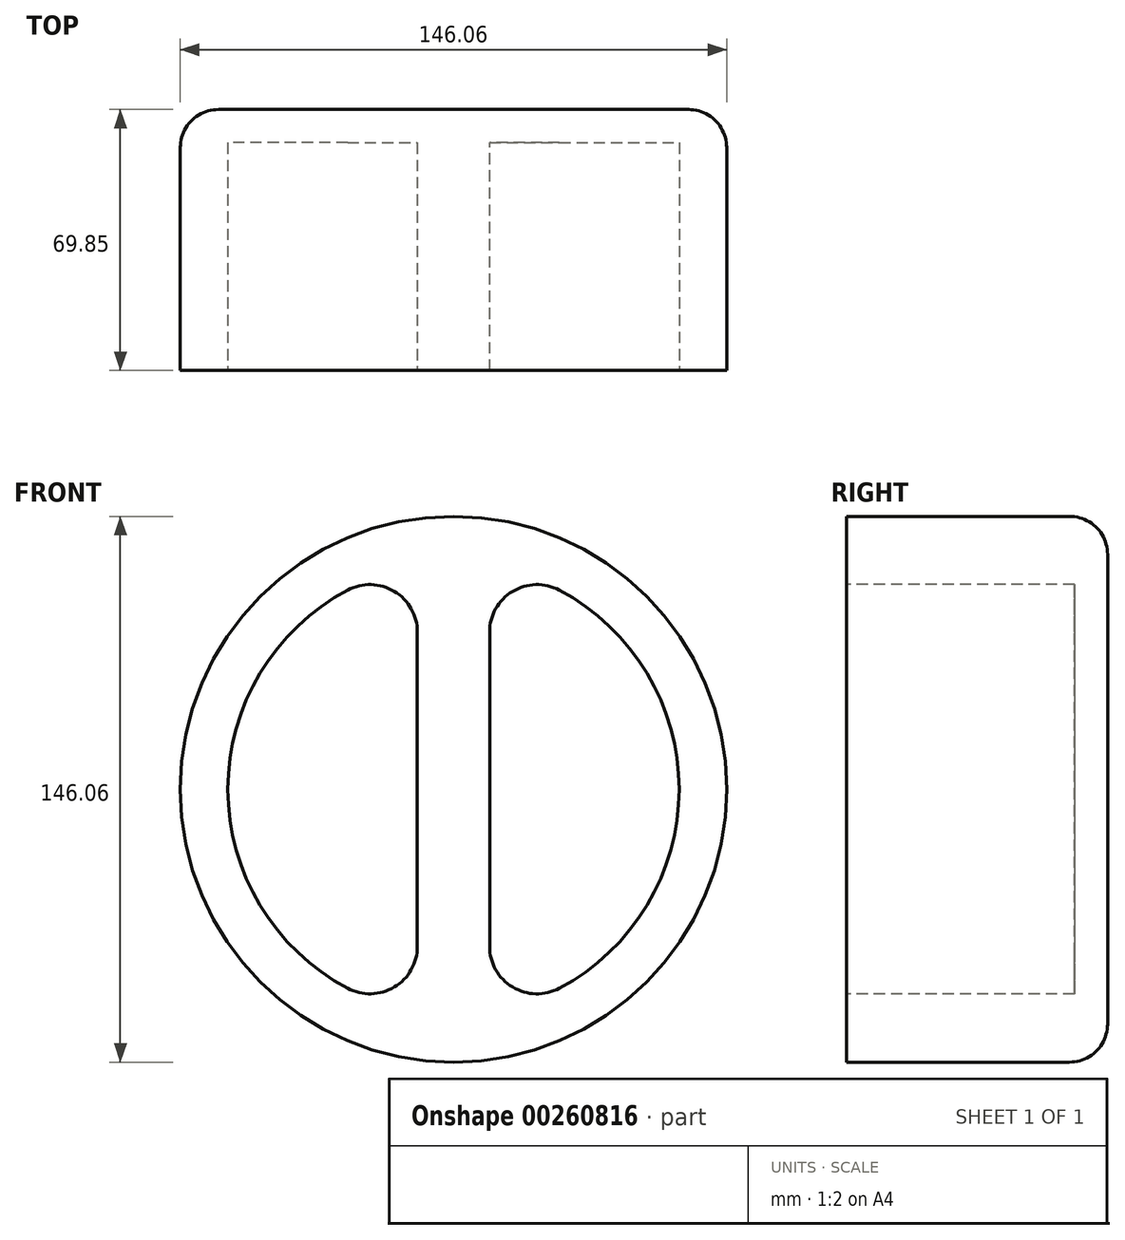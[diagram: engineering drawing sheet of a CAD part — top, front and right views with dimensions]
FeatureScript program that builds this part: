
annotation { "Feature Type Name" : "Feature", "Feature Type Description" : "" }
export const myFeature = defineFeature(function(context is Context, id is Id, definition is map)
    precondition{}
    {
        {
            var Q0;
            Q0=qCreatedBy(makeId("Front.planeOp"),FACE);
            var sketch = newSketch(context, id + "F0", { "sketchPlane" : qUnion([Q0])});
            skCircle(sketch, "E0", {"center": v(0, 0) * mm, "radius": 73.02 * mm});
            skSolve(sketch);
        }
        {
            var Q0;
            Q0=makeQuery(id+"F0.imprint","IMPRINT",FACE,{"disambiguationData":[TD([[makeQuery(id+"F0.imprint","IMPRINT",EDGE,{"derivedFrom":sQuery(id+"F0.wireOp",EDGE,"E0")}),1.0]])]});
            extrude(context, id + "F1", {"entities" : qUnion([Q0]), "depth" : 69.85 * mm});
        }
        {
            var Q0;
            Q0=makeQuery(id+"F1.opExtrude","CAP_FACE",FACE,{"disambiguationData":[OSD([sQuery(id+"F0.wireOp",EDGE,"E0")])],"isStart":false});
            var sketch = newSketch(context, id + "F2", { "sketchPlane" : qUnion([Q0])});
            skCircle(sketch, "E1", {"center": v(0, 0) * mm, "radius": 60.33 * mm});
            skLineSegment(sketch, "E2", {"start": v(-9.65, 59.55) * mm, "end": v(-9.65, -59.55) * mm});
            skLineSegment(sketch, "E3", {"start": v(9.65, 59.55) * mm, "end": v(9.65, -59.55) * mm});
            skSolve(sketch);
        }
        {
            var Q0;
            {var subQ0=sQuery(id+"F2.wireOp",EDGE,"E2");Q0=makeQuery(id+"F2.imprint","IMPRINT",FACE,{"disambiguationData":[TD([[makeQuery(id+"F2.imprint","IMPRINT",EDGE,{"derivedFrom":subQ0}),-1.0]])]});}
            var Q1;
            {var subQ0=sQuery(id+"F2.wireOp",EDGE,"E3");Q1=makeQuery(id+"F2.imprint","IMPRINT",FACE,{"disambiguationData":[TD([[makeQuery(id+"F2.imprint","IMPRINT",EDGE,{"derivedFrom":subQ0}),1.0]])]});}
            extrude(context, id + "F3", {"entities" : qUnion([Q0, Q1]), "operationType" : NewBodyOperationType.REMOVE, "oppositeDirection" : true, "depth" : 60.96 * mm});
        }
        {
            var Q0;
            {var subQ0=sQuery(id+"F2.wireOp",EDGE,"E3");var subQ1=sQuery(id+"F2.wireOp",EDGE,"E1");Q0=makeQuery(id+"F3.boolean.opBoolean","COPY",EDGE,{"derivedFrom":makeQuery(id+"F3.opExtrude","SWEPT_EDGE",EDGE,{"disambiguationData":[OSD([subQ1,subQ0]),TDD([makeQuery(id+"F2.imprint","INTERSECT",VERTEX,{"disambiguationData":[OD(0.0)],"derivedFrom":[subQ1,subQ0]})])]})});}
            var Q1;
            {var subQ0=sQuery(id+"F2.wireOp",EDGE,"E2");var subQ1=sQuery(id+"F2.wireOp",EDGE,"E1");Q1=makeQuery(id+"F3.boolean.opBoolean","COPY",EDGE,{"derivedFrom":makeQuery(id+"F3.opExtrude","SWEPT_EDGE",EDGE,{"disambiguationData":[OSD([subQ1,subQ0]),TDD([makeQuery(id+"F2.imprint","INTERSECT",VERTEX,{"disambiguationData":[OD(0.0)],"derivedFrom":[subQ1,subQ0]})])]})});}
            var Q2;
            {var subQ0=sQuery(id+"F2.wireOp",EDGE,"E3");var subQ1=sQuery(id+"F2.wireOp",EDGE,"E1");Q2=makeQuery(id+"F3.boolean.opBoolean","COPY",EDGE,{"derivedFrom":makeQuery(id+"F3.opExtrude","SWEPT_EDGE",EDGE,{"disambiguationData":[OSD([subQ1,subQ0]),TDD([makeQuery(id+"F2.imprint","INTERSECT",VERTEX,{"disambiguationData":[OD(1.0)],"derivedFrom":[subQ1,subQ0]})])]})});}
            var Q3;
            {var subQ0=sQuery(id+"F2.wireOp",EDGE,"E2");var subQ1=sQuery(id+"F2.wireOp",EDGE,"E1");Q3=makeQuery(id+"F3.boolean.opBoolean","COPY",EDGE,{"derivedFrom":makeQuery(id+"F3.opExtrude","SWEPT_EDGE",EDGE,{"disambiguationData":[OSD([subQ1,subQ0]),TDD([makeQuery(id+"F2.imprint","INTERSECT",VERTEX,{"disambiguationData":[OD(1.0)],"derivedFrom":[subQ1,subQ0]})])]})});}
            fillet(context, id + "F4", {"entities" : qUnion([Q0, Q1, Q2, Q3]), "radius" : 12.7 * mm, "tangentPropagation" : true, "allowEdgeOverflow" : false});
        }
        {
            var Q0;
            Q0=makeQuery(id+"F1.opExtrude","CAP_EDGE",EDGE,{"disambiguationData":[OSD([sQuery(id+"F0.wireOp",EDGE,"E0")])],"isStart":true});
            fillet(context, id + "F5", {"entities" : qUnion([Q0]), "radius" : 10.16 * mm, "tangentPropagation" : true, "allowEdgeOverflow" : false});
        }
    });
